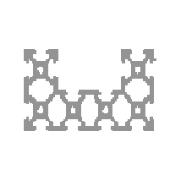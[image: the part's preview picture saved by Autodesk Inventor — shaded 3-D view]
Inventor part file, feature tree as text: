
AUTODESK INVENTOR PART (.ipt)
format: ipt  version: 2023.2 (Build 272271000, 271)  size: 1,095,168 bytes
history: native  units: mm
features: other x4, sketch x4, plane x1
ambient origin geometry x8: Origin, YZ Plane, XZ Plane, XY Plane, X Axis, Y Axis, Z Axis, Center Point
bodies: Body (feature_tree), Solid1 (feature_tree), Body1 (feature_tree)
feature tree (9):
  other  "Driven Length"
  other  "C-Beam-Extrusion.step"
  sketch  "Sketch plane"  dims[d5=0.13mm d6=0.0mm d7=90.0deg d8=700.0mm]
  other  "Start Plane"
  other  "End Plane"
  sketch  "Sketch1"  dims[d2=0.0mm]
  sketch  "Sketch2"  dims[d3=-0.0mm]
  plane  "Work Plane4"
  sketch  "Sketch3"  dims[d4=700.0mm]
